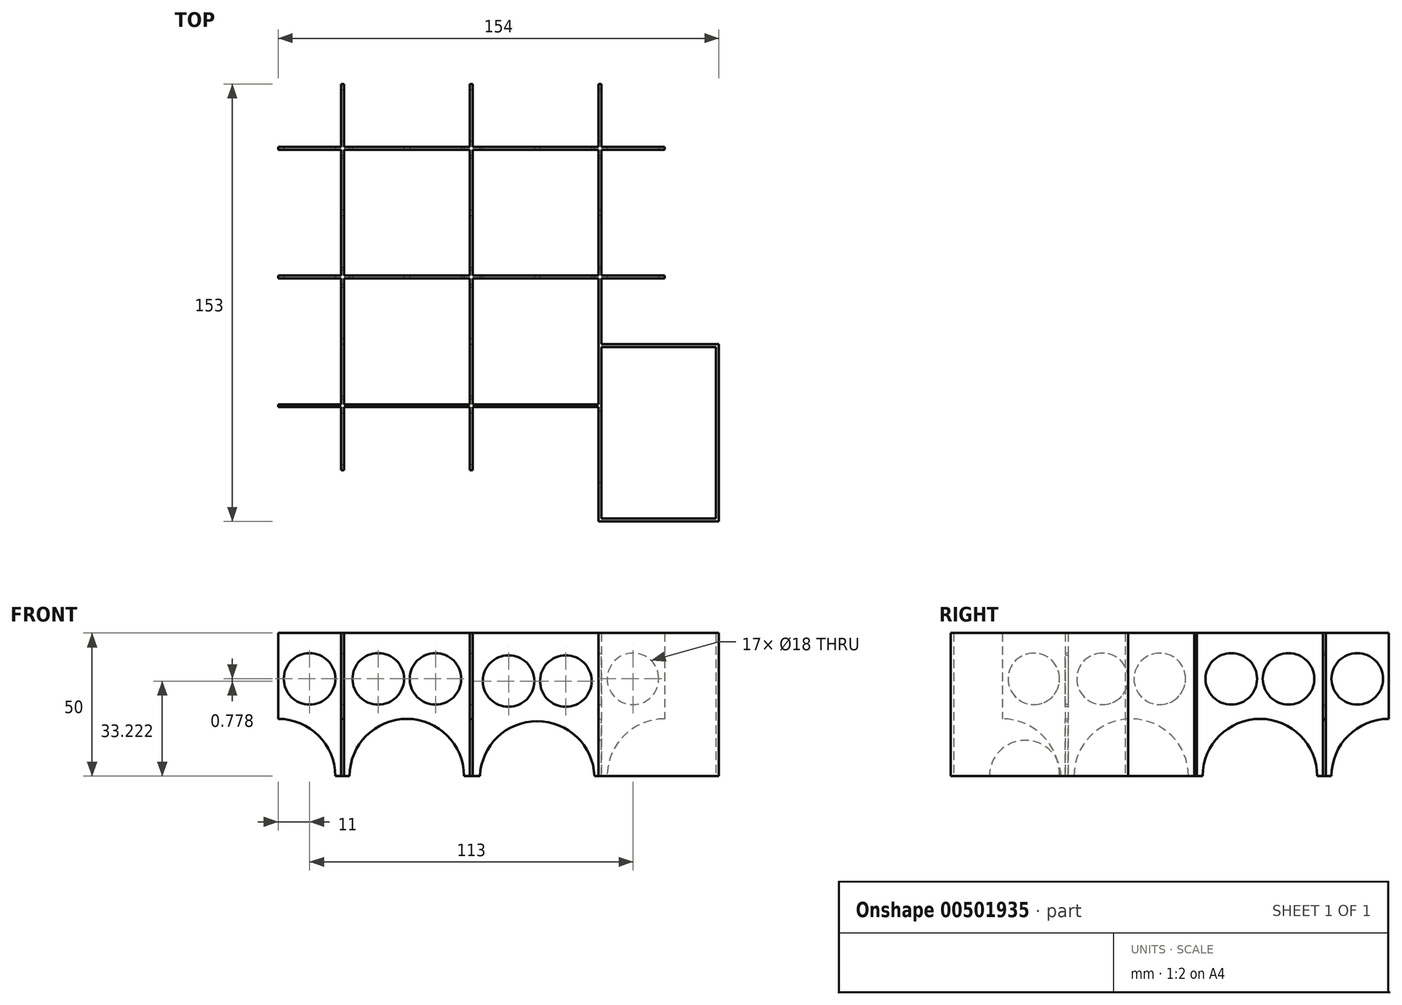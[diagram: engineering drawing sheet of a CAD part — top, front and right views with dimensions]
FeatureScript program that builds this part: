
annotation { "Feature Type Name" : "Feature", "Feature Type Description" : "" }
export const myFeature = defineFeature(function(context is Context, id is Id, definition is map)
    precondition{}
    {
        {
            var Q0;
            Q0=qCreatedBy(makeId("Top.planeOp"),FACE);
            var sketch = newSketch(context, id + "F0", { "sketchPlane" : qUnion([Q0])});
            skPoint(sketch, "E0", {"position": v(0, 45) * mm});
            skPoint(sketch, "E1", {"position": v(0, -45) * mm});
            skPoint(sketch, "E2", {"position": v(45, 0) * mm});
            skPoint(sketch, "E3", {"position": v(-45, 0) * mm});
            skLineSegment(sketch, "E4.bottom", {"start": v(-44.5, -67.5) * mm, "end": v(-45.5, -67.5) * mm});
            skLineSegment(sketch, "E4.top", {"start": v(-44.5, 67.5) * mm, "end": v(-45.5, 67.5) * mm});
            skLineSegment(sketch, "E4.left", {"start": v(-44.5, -67.5) * mm, "end": v(-44.5, 67.5) * mm});
            skLineSegment(sketch, "E4.right", {"start": v(-45.5, -67.5) * mm, "end": v(-45.5, 67.5) * mm});
            skLineSegment(sketch, "E5.bottom", {"start": v(-0.5, -67.5) * mm, "end": v(0.5, -67.5) * mm});
            skLineSegment(sketch, "E5.top", {"start": v(-0.5, 67.5) * mm, "end": v(0.5, 67.5) * mm});
            skLineSegment(sketch, "E5.left", {"start": v(-0.5, -67.5) * mm, "end": v(-0.5, 67.5) * mm});
            skLineSegment(sketch, "E5.right", {"start": v(0.5, -67.5) * mm, "end": v(0.5, 67.5) * mm});
            skPoint(sketch, "E5.middle", {"position": v(0, 0) * mm});
            skLineSegment(sketch, "E6.bottom", {"start": v(67.5, 44.5) * mm, "end": v(-67.5, 44.5) * mm});
            skLineSegment(sketch, "E6.top", {"start": v(67.5, 45.5) * mm, "end": v(-67.5, 45.5) * mm});
            skLineSegment(sketch, "E6.left", {"start": v(67.5, 44.5) * mm, "end": v(67.5, 45.5) * mm});
            skLineSegment(sketch, "E6.right", {"start": v(-67.5, 44.5) * mm, "end": v(-67.5, 45.5) * mm});
            skLineSegment(sketch, "E7.bottom", {"start": v(67.5, -0.5) * mm, "end": v(-67.5, -0.5) * mm});
            skLineSegment(sketch, "E7.top", {"start": v(67.5, 0.5) * mm, "end": v(-67.5, 0.5) * mm});
            skLineSegment(sketch, "E7.left", {"start": v(67.5, -0.5) * mm, "end": v(67.5, 0.5) * mm});
            skLineSegment(sketch, "E7.right", {"start": v(-67.5, -0.5) * mm, "end": v(-67.5, 0.5) * mm});
            skLineSegment(sketch, "E8.bottom", {"start": v(-67.5, -44.5) * mm, "end": v(44.5, -44.5) * mm});
            skLineSegment(sketch, "E8.top", {"start": v(-67.5, -45.5) * mm, "end": v(44.5, -45.5) * mm});
            skLineSegment(sketch, "E8.left", {"start": v(-67.5, -44.5) * mm, "end": v(-67.5, -45.5) * mm});
            skLineSegment(sketch, "E8.right", {"start": v(44.5, -44.5) * mm, "end": v(44.5, -45.5) * mm});
            skLineSegment(sketch, "E9", {"start": v(44.5, -45.5) * mm, "end": v(44.5, -85.5) * mm});
            skLineSegment(sketch, "E10", {"start": v(44.5, -85.5) * mm, "end": v(86.5, -85.5) * mm});
            skLineSegment(sketch, "E11", {"start": v(86.5, -85.5) * mm, "end": v(86.5, -23.5) * mm});
            skLineSegment(sketch, "E12", {"start": v(86.5, -23.5) * mm, "end": v(44.5, -23.5) * mm});
            skLineSegment(sketch, "E13", {"start": v(44.5, -44.5) * mm, "end": v(44.5, -23.5) * mm});
            skLineSegment(sketch, "E14.0", {"start": v(45.5, -44.5) * mm, "end": v(45.5, -45.5) * mm});
            skLineSegment(sketch, "E14.1", {"start": v(85.5, -24.5) * mm, "end": v(45.5, -24.5) * mm});
            skLineSegment(sketch, "E14.2", {"start": v(85.5, -84.5) * mm, "end": v(85.5, -24.5) * mm});
            skLineSegment(sketch, "E14.3", {"start": v(45.5, -44.5) * mm, "end": v(45.5, -24.5) * mm});
            skLineSegment(sketch, "E14.4", {"start": v(45.5, -84.5) * mm, "end": v(85.5, -84.5) * mm});
            skLineSegment(sketch, "E14.5", {"start": v(45.5, -45.5) * mm, "end": v(45.5, -84.5) * mm});
            skLineSegment(sketch, "E15", {"start": v(44.5, -23.5) * mm, "end": v(44.5, -0.5) * mm});
            skLineSegment(sketch, "E16", {"start": v(45.5, -23.5) * mm, "end": v(45.5, -0.5) * mm});
            skPoint(sketch, "E17", {"position": v(45, 45) * mm});
            skLineSegment(sketch, "E18", {"start": v(44.5, 44.5) * mm, "end": v(44.5, 0.5) * mm});
            skLineSegment(sketch, "E19", {"start": v(45.5, 44.5) * mm, "end": v(45.5, 0.5) * mm});
            skLineSegment(sketch, "E20", {"start": v(44.5, 45.5) * mm, "end": v(44.5, 67.5) * mm});
            skLineSegment(sketch, "E21", {"start": v(44.5, 67.5) * mm, "end": v(45.5, 67.5) * mm});
            skLineSegment(sketch, "E22", {"start": v(45.5, 67.5) * mm, "end": v(45.5, 45.5) * mm});
            skSolve(sketch);
        }
        {
            var Q0;
            {var subQ0=sQuery(id+"F0.wireOp",EDGE,"E4.top");Q0=makeQuery(id+"F0.imprint","IMPRINT",FACE,{"disambiguationData":[TD([[makeQuery(id+"F0.imprint","IMPRINT",EDGE,{"derivedFrom":subQ0}),1.0]])]});}
            var Q1;
            {var subQ5=sQuery(id+"F0.wireOp",EDGE,"E6.right");Q1=makeQuery(id+"F0.imprint","IMPRINT",FACE,{"disambiguationData":[TD([[makeQuery(id+"F0.imprint","IMPRINT",EDGE,{"derivedFrom":subQ5}),-1.0]])]});}
            var Q2;
            {var subQ0=sQuery(id+"F0.wireOp",EDGE,"E6.top");var subQ1=sQuery(id+"F0.wireOp",EDGE,"E4.left");var subQ2=makeQuery(id+"F0.imprint","INTERSECT",VERTEX,{"derivedFrom":[subQ1,subQ0]});Q2=makeQuery(id+"F0.imprint","IMPRINT",FACE,{"disambiguationData":[TD([[makeQuery(id+"F0.imprint","IMPRINT",EDGE,{"disambiguationData":[TD([[subQ2,1.0]])],"derivedFrom":subQ1}),-1.0]])]});}
            var Q3;
            {var subQ0=sQuery(id+"F0.wireOp",EDGE,"E7.top");var subQ1=sQuery(id+"F0.wireOp",EDGE,"E4.left");var subQ2=makeQuery(id+"F0.imprint","INTERSECT",VERTEX,{"derivedFrom":[subQ1,subQ0]});Q3=makeQuery(id+"F0.imprint","IMPRINT",FACE,{"disambiguationData":[TD([[makeQuery(id+"F0.imprint","IMPRINT",EDGE,{"disambiguationData":[TD([[subQ2,-1.0]])],"derivedFrom":subQ1}),1.0]])]});}
            var Q4;
            {var subQ0=sQuery(id+"F0.wireOp",EDGE,"E6.top");var subQ1=sQuery(id+"F0.wireOp",EDGE,"E4.left");var subQ2=makeQuery(id+"F0.imprint","INTERSECT",VERTEX,{"derivedFrom":[subQ1,subQ0]});Q4=makeQuery(id+"F0.imprint","IMPRINT",FACE,{"disambiguationData":[TD([[makeQuery(id+"F0.imprint","IMPRINT",EDGE,{"disambiguationData":[TD([[subQ2,1.0]])],"derivedFrom":subQ1}),1.0]])]});}
            var Q5;
            {var subQ0=sQuery(id+"F0.wireOp",EDGE,"E5.top");Q5=makeQuery(id+"F0.imprint","IMPRINT",FACE,{"disambiguationData":[TD([[makeQuery(id+"F0.imprint","IMPRINT",EDGE,{"derivedFrom":subQ0}),-1.0]])]});}
            var Q6;
            {var subQ5=sQuery(id+"F0.wireOp",EDGE,"E6.left");Q6=makeQuery(id+"F0.imprint","IMPRINT",FACE,{"disambiguationData":[TD([[makeQuery(id+"F0.imprint","IMPRINT",EDGE,{"derivedFrom":subQ5}),1.0]])]});}
            var Q7;
            {var subQ0=sQuery(id+"F0.wireOp",EDGE,"E20");Q7=makeQuery(id+"F0.imprint","IMPRINT",FACE,{"disambiguationData":[TD([[makeQuery(id+"F0.imprint","IMPRINT",EDGE,{"derivedFrom":subQ0}),-1.0]])]});}
            var Q8;
            {var subQ0=sQuery(id+"F0.wireOp",EDGE,"E6.top");var subQ1=sQuery(id+"F0.wireOp",EDGE,"E5.left");var subQ2=makeQuery(id+"F0.imprint","INTERSECT",VERTEX,{"derivedFrom":[subQ1,subQ0]});Q8=makeQuery(id+"F0.imprint","IMPRINT",FACE,{"disambiguationData":[TD([[makeQuery(id+"F0.imprint","IMPRINT",EDGE,{"disambiguationData":[TD([[subQ2,1.0]])],"derivedFrom":subQ1}),-1.0]])]});}
            var Q9;
            {var subQ0=sQuery(id+"F0.wireOp",EDGE,"E7.top");var subQ1=sQuery(id+"F0.wireOp",EDGE,"E5.left");var subQ2=makeQuery(id+"F0.imprint","INTERSECT",VERTEX,{"derivedFrom":[subQ1,subQ0]});Q9=makeQuery(id+"F0.imprint","IMPRINT",FACE,{"disambiguationData":[TD([[makeQuery(id+"F0.imprint","IMPRINT",EDGE,{"disambiguationData":[TD([[subQ2,-1.0]])],"derivedFrom":subQ1}),-1.0]])]});}
            var Q10;
            {var subQ0=sQuery(id+"F0.wireOp",EDGE,"E18");Q10=makeQuery(id+"F0.imprint","IMPRINT",FACE,{"disambiguationData":[TD([[makeQuery(id+"F0.imprint","IMPRINT",EDGE,{"derivedFrom":subQ0}),1.0]])]});}
            var Q11;
            {var subQ7=sQuery(id+"F0.wireOp",EDGE,"E7.left");Q11=makeQuery(id+"F0.imprint","IMPRINT",FACE,{"disambiguationData":[TD([[makeQuery(id+"F0.imprint","IMPRINT",EDGE,{"derivedFrom":subQ7}),1.0]])]});}
            var Q12;
            {var subQ0=sQuery(id+"F0.wireOp",EDGE,"E15");Q12=makeQuery(id+"F0.imprint","IMPRINT",FACE,{"disambiguationData":[TD([[makeQuery(id+"F0.imprint","IMPRINT",EDGE,{"derivedFrom":subQ0}),-1.0]])]});}
            var Q13;
            {var subQ0=sQuery(id+"F0.wireOp",EDGE,"E7.bottom");var subQ1=sQuery(id+"F0.wireOp",EDGE,"E5.left");var subQ2=makeQuery(id+"F0.imprint","INTERSECT",VERTEX,{"derivedFrom":[subQ1,subQ0]});Q13=makeQuery(id+"F0.imprint","IMPRINT",FACE,{"disambiguationData":[TD([[makeQuery(id+"F0.imprint","IMPRINT",EDGE,{"disambiguationData":[TD([[subQ2,-1.0]])],"derivedFrom":subQ1}),-1.0]])]});}
            var Q14;
            {var subQ0=sQuery(id+"F0.wireOp",EDGE,"E7.bottom");var subQ1=sQuery(id+"F0.wireOp",EDGE,"E4.left");var subQ2=makeQuery(id+"F0.imprint","INTERSECT",VERTEX,{"derivedFrom":[subQ1,subQ0]});Q14=makeQuery(id+"F0.imprint","IMPRINT",FACE,{"disambiguationData":[TD([[makeQuery(id+"F0.imprint","IMPRINT",EDGE,{"disambiguationData":[TD([[subQ2,-1.0]])],"derivedFrom":subQ1}),-1.0]])]});}
            var Q15;
            {var subQ0=sQuery(id+"F0.wireOp",EDGE,"E8.bottom");var subQ1=sQuery(id+"F0.wireOp",EDGE,"E5.left");var subQ2=makeQuery(id+"F0.imprint","INTERSECT",VERTEX,{"derivedFrom":[subQ1,subQ0]});Q15=makeQuery(id+"F0.imprint","IMPRINT",FACE,{"disambiguationData":[TD([[makeQuery(id+"F0.imprint","IMPRINT",EDGE,{"disambiguationData":[TD([[subQ2,-1.0]])],"derivedFrom":subQ1}),-1.0]])]});}
            var Q16;
            {var subQ5=sQuery(id+"F0.wireOp",EDGE,"E7.right");Q16=makeQuery(id+"F0.imprint","IMPRINT",FACE,{"disambiguationData":[TD([[makeQuery(id+"F0.imprint","IMPRINT",EDGE,{"derivedFrom":subQ5}),-1.0]])]});}
            var Q17;
            {var subQ0=sQuery(id+"F0.wireOp",EDGE,"E8.bottom");var subQ1=sQuery(id+"F0.wireOp",EDGE,"E4.left");var subQ2=makeQuery(id+"F0.imprint","INTERSECT",VERTEX,{"derivedFrom":[subQ1,subQ0]});Q17=makeQuery(id+"F0.imprint","IMPRINT",FACE,{"disambiguationData":[TD([[makeQuery(id+"F0.imprint","IMPRINT",EDGE,{"disambiguationData":[TD([[subQ2,-1.0]])],"derivedFrom":subQ1}),1.0]])]});}
            var Q18;
            {var subQ0=sQuery(id+"F0.wireOp",EDGE,"E7.bottom");var subQ1=sQuery(id+"F0.wireOp",EDGE,"E4.left");var subQ2=makeQuery(id+"F0.imprint","INTERSECT",VERTEX,{"derivedFrom":[subQ1,subQ0]});Q18=makeQuery(id+"F0.imprint","IMPRINT",FACE,{"disambiguationData":[TD([[makeQuery(id+"F0.imprint","IMPRINT",EDGE,{"disambiguationData":[TD([[subQ2,-1.0]])],"derivedFrom":subQ1}),1.0]])]});}
            var Q19;
            {var subQ5=sQuery(id+"F0.wireOp",EDGE,"E8.left");Q19=makeQuery(id+"F0.imprint","IMPRINT",FACE,{"disambiguationData":[TD([[makeQuery(id+"F0.imprint","IMPRINT",EDGE,{"derivedFrom":subQ5}),1.0]])]});}
            var Q20;
            {var subQ0=sQuery(id+"F0.wireOp",EDGE,"E4.bottom");Q20=makeQuery(id+"F0.imprint","IMPRINT",FACE,{"disambiguationData":[TD([[makeQuery(id+"F0.imprint","IMPRINT",EDGE,{"derivedFrom":subQ0}),-1.0]])]});}
            var Q21;
            {var subQ0=sQuery(id+"F0.wireOp",EDGE,"E8.top");var subQ1=sQuery(id+"F0.wireOp",EDGE,"E4.left");var subQ2=makeQuery(id+"F0.imprint","INTERSECT",VERTEX,{"derivedFrom":[subQ1,subQ0]});Q21=makeQuery(id+"F0.imprint","IMPRINT",FACE,{"disambiguationData":[TD([[makeQuery(id+"F0.imprint","IMPRINT",EDGE,{"disambiguationData":[TD([[subQ2,-1.0]])],"derivedFrom":subQ1}),1.0]])]});}
            var Q22;
            {var subQ0=sQuery(id+"F0.wireOp",EDGE,"E8.top");var subQ1=sQuery(id+"F0.wireOp",EDGE,"E4.left");var subQ2=makeQuery(id+"F0.imprint","INTERSECT",VERTEX,{"derivedFrom":[subQ1,subQ0]});Q22=makeQuery(id+"F0.imprint","IMPRINT",FACE,{"disambiguationData":[TD([[makeQuery(id+"F0.imprint","IMPRINT",EDGE,{"disambiguationData":[TD([[subQ2,-1.0]])],"derivedFrom":subQ1}),-1.0]])]});}
            var Q23;
            {var subQ0=sQuery(id+"F0.wireOp",EDGE,"E5.bottom");Q23=makeQuery(id+"F0.imprint","IMPRINT",FACE,{"disambiguationData":[TD([[makeQuery(id+"F0.imprint","IMPRINT",EDGE,{"derivedFrom":subQ0}),1.0]])]});}
            var Q24;
            {var subQ5=sQuery(id+"F0.wireOp",EDGE,"E8.right");Q24=makeQuery(id+"F0.imprint","IMPRINT",FACE,{"disambiguationData":[TD([[makeQuery(id+"F0.imprint","IMPRINT",EDGE,{"derivedFrom":subQ5}),-1.0]])]});}
            var Q25;
            {var subQ0=sQuery(id+"F0.wireOp",EDGE,"E8.top");var subQ1=sQuery(id+"F0.wireOp",EDGE,"E5.left");var subQ2=makeQuery(id+"F0.imprint","INTERSECT",VERTEX,{"derivedFrom":[subQ1,subQ0]});Q25=makeQuery(id+"F0.imprint","IMPRINT",FACE,{"disambiguationData":[TD([[makeQuery(id+"F0.imprint","IMPRINT",EDGE,{"disambiguationData":[TD([[subQ2,-1.0]])],"derivedFrom":subQ1}),-1.0]])]});}
            var Q26;
            Q26=makeQuery(id+"F0.imprint","IMPRINT",FACE,{"disambiguationData":[TD([[makeQuery(id+"F0.imprint","IMPRINT",EDGE,{"derivedFrom":sQuery(id+"F0.wireOp",EDGE,"E8.right")}),1.0]])]});
            extrude(context, id + "F1", {"entities" : qUnion([Q0, Q1, Q2, Q3, Q4, Q5, Q6, Q7, Q8, Q9, Q10, Q11, Q12, Q13, Q14, Q15, Q16, Q17, Q18, Q19, Q20, Q21, Q22, Q23, Q24, Q25, Q26]), "depth" : 50 * mm});
        }
        {
            var Q0;
            {var subQ0=sQuery(id+"F0.wireOp",EDGE,"E8.top");Q0=makeQuery(id+"F1.opExtrude","SWEPT_FACE",FACE,{"disambiguationData":[OSD([subQ0]),TDD([makeQuery(id+"F0.imprint","IMPRINT",EDGE,{"disambiguationData":[TD([[makeQuery(id+"F0.imprint","INTERSECT",VERTEX,{"derivedFrom":[sQuery(id+"F0.wireOp",EDGE,"E4.left"),subQ0]}),-1.0]])],"derivedFrom":subQ0})])]});}
            var sketch = newSketch(context, id + "F2", { "sketchPlane" : qUnion([Q0])});
            skPoint(sketch, "E23", {"position": v(-22.5, 0) * mm});
            skCircle(sketch, "E24", {"center": v(-22.5, 0) * mm, "radius": 20 * mm});
            skPoint(sketch, "E25", {"position": v(-32.5, 34) * mm});
            skPoint(sketch, "E26", {"position": v(-12.5, 34) * mm});
            skCircle(sketch, "E27", {"center": v(-32.5, 34) * mm, "radius": 9 * mm});
            skCircle(sketch, "E28", {"center": v(-12.5, 34) * mm, "radius": 9 * mm});
            skSolve(sketch);
        }
        {
            var Q0;
            Q0=makeQuery(id+"F2.imprint","IMPRINT",FACE,{"disambiguationData":[TD([[makeQuery(id+"F2.imprint","IMPRINT",EDGE,{"derivedFrom":sQuery(id+"F2.wireOp",EDGE,"E27")}),1.0]])]});
            var Q1;
            Q1=makeQuery(id+"F2.imprint","IMPRINT",FACE,{"disambiguationData":[TD([[makeQuery(id+"F2.imprint","IMPRINT",EDGE,{"derivedFrom":sQuery(id+"F2.wireOp",EDGE,"E28")}),1.0]])]});
            var Q2;
            {var subQ0=sQuery(id+"F2.wireOp",EDGE,"E24");var subQ1=sQuery(id+"F0.wireOp",EDGE,"E8.top");var subQ2=makeQuery(id+"F1.opExtrude","CAP_EDGE",EDGE,{"disambiguationData":[OSD([subQ1]),TDD([makeQuery(id+"F0.imprint","IMPRINT",EDGE,{"disambiguationData":[TD([[makeQuery(id+"F0.imprint","INTERSECT",VERTEX,{"derivedFrom":[sQuery(id+"F0.wireOp",EDGE,"E4.left"),subQ1]}),-1.0]])],"derivedFrom":subQ1})])],"isStart":true});var subQ3=makeQuery(id+"F2.imprint","INTERSECT",VERTEX,{"disambiguationData":[OD(0.0)],"derivedFrom":[subQ2,subQ0]});Q2=makeQuery(id+"F2.imprint","IMPRINT",FACE,{"disambiguationData":[TD([[makeQuery(id+"F2.imprint","IMPRINT",EDGE,{"disambiguationData":[TD([[subQ3,1.0]])],"derivedFrom":subQ0}),1.0]])]});}
            extrude(context, id + "F3", {"entities" : qUnion([Q0, Q1, Q2]), "operationType" : NewBodyOperationType.REMOVE, "oppositeDirection" : true, "depth" : 500 * mm});
        }
        {
            var Q0;
            {var subQ0=sQuery(id+"F0.wireOp",EDGE,"E8.top");Q0=makeQuery(id+"F1.opExtrude","SWEPT_FACE",FACE,{"disambiguationData":[OSD([subQ0]),TDD([makeQuery(id+"F0.imprint","IMPRINT",EDGE,{"disambiguationData":[TD([[makeQuery(id+"F0.imprint","INTERSECT",VERTEX,{"derivedFrom":[sQuery(id+"F0.wireOp",EDGE,"E5.right"),subQ0]}),-1.0]])],"derivedFrom":subQ0})])]});}
            var sketch = newSketch(context, id + "F4", { "sketchPlane" : qUnion([Q0])});
            skPoint(sketch, "E29", {"position": v(23.04, -0.78) * mm});
            skCircle(sketch, "E30", {"center": v(23.04, -0.78) * mm, "radius": 20 * mm});
            skPoint(sketch, "E31", {"position": v(13.04, 33.22) * mm});
            skPoint(sketch, "E32", {"position": v(33.04, 33.22) * mm});
            skCircle(sketch, "E33", {"center": v(13.04, 33.22) * mm, "radius": 9 * mm});
            skCircle(sketch, "E34", {"center": v(33.04, 33.22) * mm, "radius": 9 * mm});
            skSolve(sketch);
        }
        {
            var Q0;
            Q0=makeQuery(id+"F4.imprint","IMPRINT",FACE,{"disambiguationData":[TD([[makeQuery(id+"F4.imprint","IMPRINT",EDGE,{"derivedFrom":sQuery(id+"F4.wireOp",EDGE,"E33")}),1.0]])]});
            var Q1;
            Q1=makeQuery(id+"F4.imprint","IMPRINT",FACE,{"disambiguationData":[TD([[makeQuery(id+"F4.imprint","IMPRINT",EDGE,{"derivedFrom":sQuery(id+"F4.wireOp",EDGE,"E34")}),1.0]])]});
            var Q2;
            {var subQ0=sQuery(id+"F4.wireOp",EDGE,"E30");var subQ1=sQuery(id+"F0.wireOp",EDGE,"E8.top");var subQ2=makeQuery(id+"F1.opExtrude","CAP_EDGE",EDGE,{"disambiguationData":[OSD([subQ1]),TDD([makeQuery(id+"F0.imprint","IMPRINT",EDGE,{"disambiguationData":[TD([[makeQuery(id+"F0.imprint","INTERSECT",VERTEX,{"derivedFrom":[sQuery(id+"F0.wireOp",EDGE,"E5.right"),subQ1]}),-1.0]])],"derivedFrom":subQ1})])],"isStart":true});var subQ3=makeQuery(id+"F4.imprint","INTERSECT",VERTEX,{"disambiguationData":[OD(0.0)],"derivedFrom":[subQ2,subQ0]});Q2=makeQuery(id+"F4.imprint","IMPRINT",FACE,{"disambiguationData":[TD([[makeQuery(id+"F4.imprint","IMPRINT",EDGE,{"disambiguationData":[TD([[subQ3,-1.0]])],"derivedFrom":subQ0}),1.0]])]});}
            extrude(context, id + "F5", {"entities" : qUnion([Q0, Q1, Q2]), "operationType" : NewBodyOperationType.REMOVE, "oppositeDirection" : true, "depth" : 500 * mm});
        }
        {
            var Q0;
            {var subQ0=sQuery(id+"F0.wireOp",EDGE,"E8.top");Q0=makeQuery(id+"F1.opExtrude","SWEPT_FACE",FACE,{"disambiguationData":[OSD([subQ0]),TDD([makeQuery(id+"F0.imprint","IMPRINT",EDGE,{"disambiguationData":[TD([[makeQuery(id+"F0.imprint","INTERSECT",VERTEX,{"derivedFrom":[subQ0,sQuery(id+"F0.wireOp",EDGE,"E8.left")]}),-1.0]])],"derivedFrom":subQ0})])]});}
            var sketch = newSketch(context, id + "F6", { "sketchPlane" : qUnion([Q0])});
            skCircle(sketch, "E35", {"center": v(-67.5, 0) * mm, "radius": 20 * mm});
            skPoint(sketch, "E36", {"position": v(-56.5, 34) * mm});
            skCircle(sketch, "E37", {"center": v(-56.5, 34) * mm, "radius": 9 * mm});
            skSolve(sketch);
        }
        {
            var Q0;
            Q0=makeQuery(id+"F6.imprint","IMPRINT",FACE,{"disambiguationData":[TD([[makeQuery(id+"F6.imprint","IMPRINT",EDGE,{"derivedFrom":sQuery(id+"F6.wireOp",EDGE,"E37")}),1.0]])]});
            var Q1;
            {var subQ0=sQuery(id+"F6.wireOp",EDGE,"E35");var subQ1=sQuery(id+"F0.wireOp",EDGE,"E8.left");var subQ2=sQuery(id+"F0.wireOp",EDGE,"E8.top");var subQ3=makeQuery(id+"F1.opExtrude","SWEPT_EDGE",EDGE,{"disambiguationData":[OSD([subQ2,subQ1])]});var subQ4=makeQuery(id+"F6.imprint","INTERSECT",VERTEX,{"derivedFrom":[subQ3,subQ0]});Q1=makeQuery(id+"F6.imprint","IMPRINT",FACE,{"disambiguationData":[TD([[makeQuery(id+"F6.imprint","IMPRINT",EDGE,{"disambiguationData":[TD([[subQ4,1.0]])],"derivedFrom":subQ0}),1.0]])]});}
            extrude(context, id + "F7", {"entities" : qUnion([Q0, Q1]), "operationType" : NewBodyOperationType.REMOVE, "oppositeDirection" : true, "depth" : 500 * mm});
        }
        {
            var Q0;
            {var subQ0=sQuery(id+"F0.wireOp",EDGE,"E5.right");Q0=makeQuery(id+"F1.opExtrude","SWEPT_FACE",FACE,{"disambiguationData":[OSD([subQ0]),TDD([makeQuery(id+"F0.imprint","IMPRINT",EDGE,{"disambiguationData":[TD([[makeQuery(id+"F0.imprint","INTERSECT",VERTEX,{"derivedFrom":[subQ0,sQuery(id+"F0.wireOp",EDGE,"E8.bottom")]}),-1.0]])],"derivedFrom":subQ0})])]});}
            var sketch = newSketch(context, id + "F8", { "sketchPlane" : qUnion([Q0])});
            skPoint(sketch, "E38", {"position": v(-22.5, 0) * mm});
            skCircle(sketch, "E39", {"center": v(-22.5, 0) * mm, "radius": 20 * mm});
            skPoint(sketch, "E40", {"position": v(-32.5, 34) * mm});
            skPoint(sketch, "E41", {"position": v(-12.5, 34) * mm});
            skCircle(sketch, "E42", {"center": v(-32.5, 34) * mm, "radius": 9 * mm});
            skCircle(sketch, "E43", {"center": v(-12.5, 34) * mm, "radius": 9 * mm});
            skSolve(sketch);
        }
        {
            var Q0;
            Q0=makeQuery(id+"F8.imprint","IMPRINT",FACE,{"disambiguationData":[TD([[makeQuery(id+"F8.imprint","IMPRINT",EDGE,{"derivedFrom":sQuery(id+"F8.wireOp",EDGE,"E43")}),1.0]])]});
            var Q1;
            {var subQ0=sQuery(id+"F8.wireOp",EDGE,"E39");var subQ1=sQuery(id+"F0.wireOp",EDGE,"E5.right");var subQ2=makeQuery(id+"F1.opExtrude","CAP_EDGE",EDGE,{"disambiguationData":[OSD([subQ1]),TDD([makeQuery(id+"F0.imprint","IMPRINT",EDGE,{"disambiguationData":[TD([[makeQuery(id+"F0.imprint","INTERSECT",VERTEX,{"derivedFrom":[subQ1,sQuery(id+"F0.wireOp",EDGE,"E8.bottom")]}),-1.0]])],"derivedFrom":subQ1})])],"isStart":true});var subQ3=makeQuery(id+"F8.imprint","INTERSECT",VERTEX,{"disambiguationData":[OD(0.0)],"derivedFrom":[subQ2,subQ0]});Q1=makeQuery(id+"F8.imprint","IMPRINT",FACE,{"disambiguationData":[TD([[makeQuery(id+"F8.imprint","IMPRINT",EDGE,{"disambiguationData":[TD([[subQ3,1.0]])],"derivedFrom":subQ0}),1.0]])]});}
            var Q2;
            Q2=makeQuery(id+"F8.imprint","IMPRINT",FACE,{"disambiguationData":[TD([[makeQuery(id+"F8.imprint","IMPRINT",EDGE,{"derivedFrom":sQuery(id+"F8.wireOp",EDGE,"E42")}),1.0]])]});
            extrude(context, id + "F9", {"entities" : qUnion([Q0, Q1, Q2]), "operationType" : NewBodyOperationType.REMOVE, "oppositeDirection" : true, "depth" : 500 * mm});
        }
        {
            var Q0;
            {var subQ0=sQuery(id+"F0.wireOp",EDGE,"E5.right");Q0=makeQuery(id+"F1.opExtrude","SWEPT_FACE",FACE,{"disambiguationData":[OSD([subQ0]),TDD([makeQuery(id+"F0.imprint","IMPRINT",EDGE,{"disambiguationData":[TD([[makeQuery(id+"F0.imprint","INTERSECT",VERTEX,{"derivedFrom":[sQuery(id+"F0.wireOp",EDGE,"E5.bottom"),subQ0]}),-1.0]])],"derivedFrom":subQ0})])]});}
            var sketch = newSketch(context, id + "F10", { "sketchPlane" : qUnion([Q0])});
            skCircle(sketch, "E44", {"center": v(-67.5, 0) * mm, "radius": 20 * mm});
            skPoint(sketch, "E45", {"position": v(-56.5, 34) * mm});
            skCircle(sketch, "E46", {"center": v(-56.5, 34) * mm, "radius": 9 * mm});
            skSolve(sketch);
        }
        {
            var Q0;
            Q0=makeQuery(id+"F10.imprint","IMPRINT",FACE,{"disambiguationData":[TD([[makeQuery(id+"F10.imprint","IMPRINT",EDGE,{"derivedFrom":sQuery(id+"F10.wireOp",EDGE,"E46")}),1.0]])]});
            var Q1;
            {var subQ0=sQuery(id+"F10.wireOp",EDGE,"E44");var subQ1=sQuery(id+"F0.wireOp",EDGE,"E5.right");var subQ2=sQuery(id+"F0.wireOp",EDGE,"E5.bottom");var subQ3=makeQuery(id+"F1.opExtrude","SWEPT_EDGE",EDGE,{"disambiguationData":[OSD([subQ2,subQ1])]});var subQ4=makeQuery(id+"F10.imprint","INTERSECT",VERTEX,{"derivedFrom":[subQ3,subQ0]});Q1=makeQuery(id+"F10.imprint","IMPRINT",FACE,{"disambiguationData":[TD([[makeQuery(id+"F10.imprint","IMPRINT",EDGE,{"disambiguationData":[TD([[subQ4,1.0]])],"derivedFrom":subQ0}),1.0]])]});}
            extrude(context, id + "F11", {"entities" : qUnion([Q0, Q1]), "operationType" : NewBodyOperationType.REMOVE, "oppositeDirection" : true, "depth" : 500 * mm});
        }
        {
            var Q0;
            Q0=makeQuery(id+"F1.opExtrude","SWEPT_FACE",FACE,{"disambiguationData":[OSD([sQuery(id+"F0.wireOp",EDGE,"E19")])]});
            var sketch = newSketch(context, id + "F12", { "sketchPlane" : qUnion([Q0])});
            skPoint(sketch, "E47", {"position": v(22.5, 0) * mm});
            skCircle(sketch, "E48", {"center": v(22.5, 0) * mm, "radius": 20 * mm});
            skPoint(sketch, "E49", {"position": v(12.5, 34) * mm});
            skPoint(sketch, "E50", {"position": v(32.5, 34) * mm});
            skCircle(sketch, "E51", {"center": v(12.5, 34) * mm, "radius": 9 * mm});
            skCircle(sketch, "E52", {"center": v(32.5, 34) * mm, "radius": 9 * mm});
            skSolve(sketch);
        }
        {
            var Q0;
            Q0=makeQuery(id+"F12.imprint","IMPRINT",FACE,{"disambiguationData":[TD([[makeQuery(id+"F12.imprint","IMPRINT",EDGE,{"derivedFrom":sQuery(id+"F12.wireOp",EDGE,"E51")}),1.0]])]});
            var Q1;
            Q1=makeQuery(id+"F12.imprint","IMPRINT",FACE,{"disambiguationData":[TD([[makeQuery(id+"F12.imprint","IMPRINT",EDGE,{"derivedFrom":sQuery(id+"F12.wireOp",EDGE,"E52")}),1.0]])]});
            var Q2;
            {var subQ0=sQuery(id+"F12.wireOp",EDGE,"E48");var subQ1=makeQuery(id+"F1.opExtrude","CAP_EDGE",EDGE,{"disambiguationData":[OSD([sQuery(id+"F0.wireOp",EDGE,"E19")])],"isStart":true});var subQ2=makeQuery(id+"F12.imprint","INTERSECT",VERTEX,{"disambiguationData":[OD(0.0)],"derivedFrom":[subQ1,subQ0]});Q2=makeQuery(id+"F12.imprint","IMPRINT",FACE,{"disambiguationData":[TD([[makeQuery(id+"F12.imprint","IMPRINT",EDGE,{"disambiguationData":[TD([[subQ2,-1.0]])],"derivedFrom":subQ0}),1.0]])]});}
            extrude(context, id + "F13", {"entities" : qUnion([Q0, Q1, Q2]), "operationType" : NewBodyOperationType.REMOVE, "oppositeDirection" : true, "depth" : 500 * mm});
        }
        {
            var Q0;
            Q0=makeQuery(id+"F1.opExtrude","SWEPT_FACE",FACE,{"disambiguationData":[OSD([sQuery(id+"F0.wireOp",EDGE,"E22")])]});
            var sketch = newSketch(context, id + "F14", { "sketchPlane" : qUnion([Q0])});
            skCircle(sketch, "E53", {"center": v(67.5, 0) * mm, "radius": 20 * mm});
            skPoint(sketch, "E54", {"position": v(56.5, 34) * mm});
            skCircle(sketch, "E55", {"center": v(56.5, 34) * mm, "radius": 9 * mm});
            skSolve(sketch);
        }
        {
            var Q0;
            {var subQ0=sQuery(id+"F14.wireOp",EDGE,"E53");var subQ1=sQuery(id+"F0.wireOp",EDGE,"E22");var subQ4=makeQuery(id+"F1.opExtrude","CAP_EDGE",EDGE,{"disambiguationData":[OSD([subQ1])],"isStart":true});var subQ5=makeQuery(id+"F14.imprint","INTERSECT",VERTEX,{"derivedFrom":[subQ4,subQ0]});Q0=makeQuery(id+"F14.imprint","IMPRINT",FACE,{"disambiguationData":[TD([[makeQuery(id+"F14.imprint","IMPRINT",EDGE,{"disambiguationData":[TD([[subQ5,1.0]])],"derivedFrom":subQ0}),1.0]])]});}
            var Q1;
            Q1=makeQuery(id+"F14.imprint","IMPRINT",FACE,{"disambiguationData":[TD([[makeQuery(id+"F14.imprint","IMPRINT",EDGE,{"derivedFrom":sQuery(id+"F14.wireOp",EDGE,"E55")}),1.0]])]});
            extrude(context, id + "F15", {"entities" : qUnion([Q0, Q1]), "operationType" : NewBodyOperationType.REMOVE, "oppositeDirection" : true, "depth" : 500 * mm});
        }
        {
            var Q0;
            {var subQ0=sQuery(id+"F0.wireOp",EDGE,"E7.bottom");Q0=makeQuery(id+"F1.opExtrude","SWEPT_FACE",FACE,{"disambiguationData":[OSD([subQ0]),TDD([makeQuery(id+"F0.imprint","IMPRINT",EDGE,{"disambiguationData":[TD([[makeQuery(id+"F0.imprint","INTERSECT",VERTEX,{"derivedFrom":[subQ0,sQuery(id+"F0.wireOp",EDGE,"E7.left")]}),-1.0]])],"derivedFrom":subQ0})])]});}
            var sketch = newSketch(context, id + "F16", { "sketchPlane" : qUnion([Q0])});
            skCircle(sketch, "E56", {"center": v(67.5, 0) * mm, "radius": 20 * mm});
            skPoint(sketch, "E57", {"position": v(56.5, 34) * mm});
            skCircle(sketch, "E58", {"center": v(56.5, 34) * mm, "radius": 9 * mm});
            skSolve(sketch);
        }
        {
            var Q0;
            Q0=makeQuery(id+"F16.imprint","IMPRINT",FACE,{"disambiguationData":[TD([[makeQuery(id+"F16.imprint","IMPRINT",EDGE,{"derivedFrom":sQuery(id+"F16.wireOp",EDGE,"E58")}),1.0]])]});
            var Q1;
            {var subQ0=sQuery(id+"F16.wireOp",EDGE,"E56");var subQ1=sQuery(id+"F0.wireOp",EDGE,"E7.left");var subQ2=sQuery(id+"F0.wireOp",EDGE,"E7.bottom");var subQ3=makeQuery(id+"F1.opExtrude","SWEPT_EDGE",EDGE,{"disambiguationData":[OSD([subQ2,subQ1])]});var subQ4=makeQuery(id+"F16.imprint","INTERSECT",VERTEX,{"derivedFrom":[subQ3,subQ0]});Q1=makeQuery(id+"F16.imprint","IMPRINT",FACE,{"disambiguationData":[TD([[makeQuery(id+"F16.imprint","IMPRINT",EDGE,{"disambiguationData":[TD([[subQ4,-1.0]])],"derivedFrom":subQ0}),1.0]])]});}
            extrude(context, id + "F17", {"entities" : qUnion([Q0, Q1]), "operationType" : NewBodyOperationType.REMOVE, "oppositeDirection" : true, "depth" : 400 * mm});
        }
        {
            var Q0;
            Q0=makeQuery(id+"F1.opExtrude","SWEPT_FACE",FACE,{"disambiguationData":[OSD([sQuery(id+"F0.wireOp",EDGE,"E13"),sQuery(id+"F0.wireOp",EDGE,"E15")])]});
            var sketch = newSketch(context, id + "F18", { "sketchPlane" : qUnion([Q0])});
            skPoint(sketch, "E59", {"position": v(34, 0) * mm});
            skCircle(sketch, "E60", {"center": v(34, 0) * mm, "radius": 9.75 * mm});
            skPoint(sketch, "E61", {"position": v(59.5, 0) * mm});
            skCircle(sketch, "E62", {"center": v(59.5, 0) * mm, "radius": 12.5 * mm});
            skSolve(sketch);
        }
        {
            var Q0;
            {var subQ0=sQuery(id+"F18.wireOp",EDGE,"E60");var subQ1=makeQuery(id+"F1.opExtrude","CAP_EDGE",EDGE,{"disambiguationData":[OSD([sQuery(id+"F0.wireOp",EDGE,"E13"),sQuery(id+"F0.wireOp",EDGE,"E15")])],"isStart":true});var subQ2=makeQuery(id+"F18.imprint","INTERSECT",VERTEX,{"disambiguationData":[OD(0.0)],"derivedFrom":[subQ1,subQ0]});Q0=makeQuery(id+"F18.imprint","IMPRINT",FACE,{"disambiguationData":[TD([[makeQuery(id+"F18.imprint","IMPRINT",EDGE,{"disambiguationData":[TD([[subQ2,-1.0]])],"derivedFrom":subQ0}),1.0]])]});}
            var Q1;
            Q1=makeQuery(id+"F18.imprint","IMPRINT",FACE,{"disambiguationData":[TD([[makeQuery(id+"F18.imprint","IMPRINT",EDGE,{"derivedFrom":sQuery(id+"F18.wireOp",EDGE,"E62")}),1.0]])]});
            extrude(context, id + "F19", {"entities" : qUnion([Q0, Q1]), "operationType" : NewBodyOperationType.REMOVE, "oppositeDirection" : true, "depth" : 1 * mm});
        }
    });
